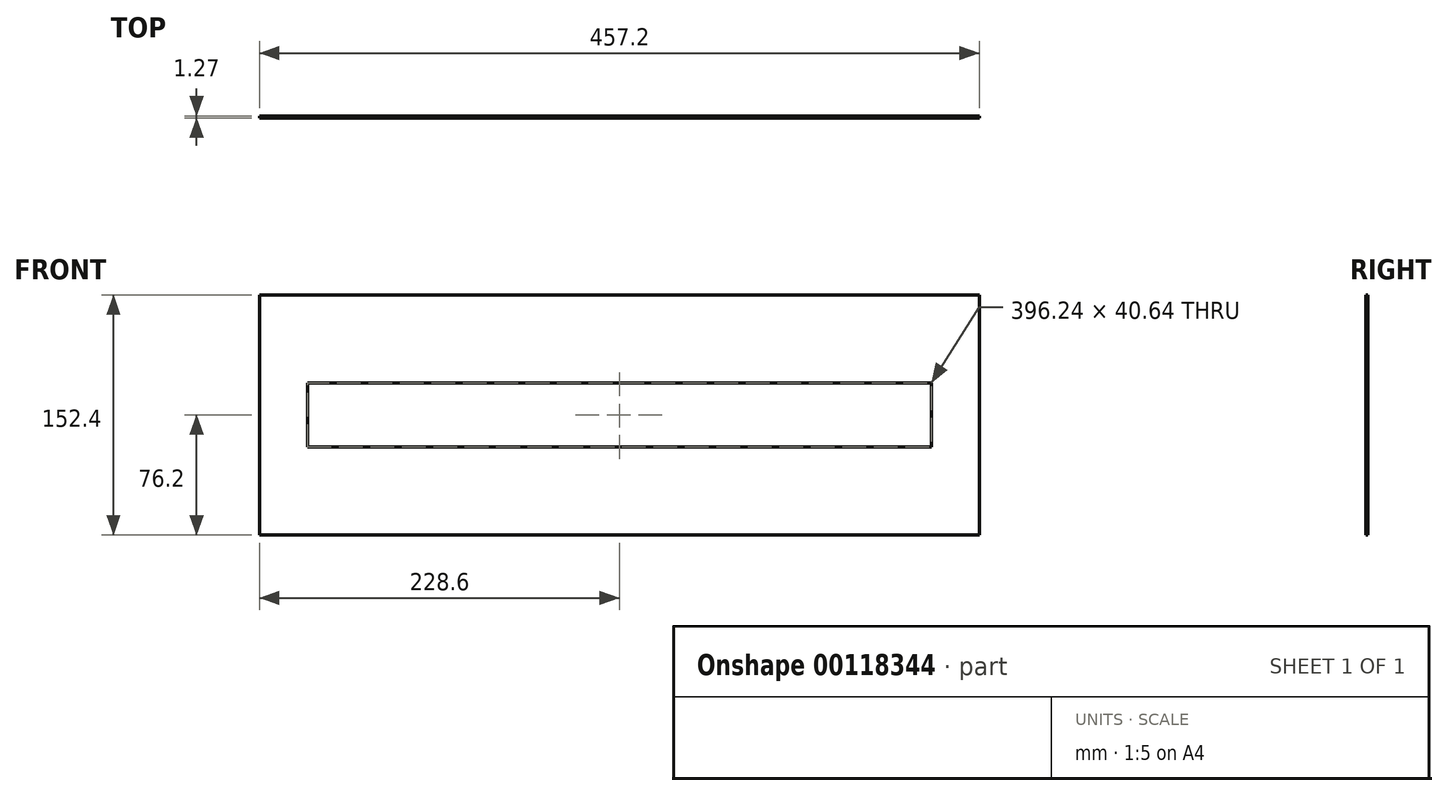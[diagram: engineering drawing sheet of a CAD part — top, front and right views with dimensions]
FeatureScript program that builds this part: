
annotation { "Feature Type Name" : "Feature", "Feature Type Description" : "" }
export const myFeature = defineFeature(function(context is Context, id is Id, definition is map)
    precondition{}
    {
        {
            var Q0;
            Q0=qCreatedBy(makeId("Front.planeOp"),FACE);
            var sketch = newSketch(context, id + "F0", { "sketchPlane" : qUnion([Q0])});
            skLineSegment(sketch, "E0.bottom", {"start": v(-228.6, 76.2) * mm, "end": v(228.6, 76.2) * mm});
            skLineSegment(sketch, "E0.top", {"start": v(-228.6, -76.2) * mm, "end": v(228.6, -76.2) * mm});
            skLineSegment(sketch, "E0.left", {"start": v(-228.6, 76.2) * mm, "end": v(-228.6, -76.2) * mm});
            skLineSegment(sketch, "E0.right", {"start": v(228.6, 76.2) * mm, "end": v(228.6, -76.2) * mm});
            skPoint(sketch, "E0.middle", {"position": v(0, 0) * mm});
            skSolve(sketch);
        }
        {
            var Q0;
            Q0 = qSketchRegion(id + "F0", true);
            extrude(context, id + "F1", {"entities" : qUnion([Q0]), "depth" : 1.27 * mm});
        }
        {
            var Q0;
            Q0=makeQuery(id+"F1.opExtrude","CAP_FACE",FACE,{"disambiguationData":[OSD([sQuery(id+"F0.wireOp",EDGE,"E0.bottom"),sQuery(id+"F0.wireOp",EDGE,"E0.top"),sQuery(id+"F0.wireOp",EDGE,"E0.left"),sQuery(id+"F0.wireOp",EDGE,"E0.right")])],"isStart":false});
            var sketch = newSketch(context, id + "F2", { "sketchPlane" : qUnion([Q0])});
            skLineSegment(sketch, "E1.bottom", {"start": v(198.12, 20.32) * mm, "end": v(-198.12, 20.32) * mm});
            skLineSegment(sketch, "E1.top", {"start": v(198.12, -20.32) * mm, "end": v(-198.12, -20.32) * mm});
            skLineSegment(sketch, "E1.left", {"start": v(198.12, 20.32) * mm, "end": v(198.12, -20.32) * mm});
            skLineSegment(sketch, "E1.right", {"start": v(-198.12, 20.32) * mm, "end": v(-198.12, -20.32) * mm});
            skPoint(sketch, "E1.middle", {"position": v(0, 0) * mm});
            skSolve(sketch);
        }
        {
            var Q0;
            Q0 = qSketchRegion(id + "F2", true);
            extrude(context, id + "F3", {"entities" : qUnion([Q0]), "operationType" : NewBodyOperationType.REMOVE, "oppositeDirection" : true, "depth" : 25.4 * mm});
        }
    });
